# Revit family: Deca_Ducha Higienica com Derivacao_Ducha Activa Competitivo_1948.ACT.CR
name_source: partatom
category: Plumbing Fixtures
units: mm (PartAtom-declared; Revit-internal decimal feet)

## family parameters
Cut with Voids When Loaded = No
Host = Face
Part Type = Normal
Room Calculation Point = No
Round Connector Dimension = Use Radius
Shared = No

## types (2) — shared parameters
Acompanha o Produto = Acompanha Parfuso e Bucha para fixação + Deca confort
Aprovado por = quattroD
Atendimento ao Cliente = 0800-0117073
Categoria = METAIS PARA BANHEIRO
Composição Anel Vedação = -
Composição Assento = -
Composição Básica = Liga cobre (bronze e latão),Aço,Plástico de Engenharia,Elastômeros
Composição Componente = -
Consumo = -
Cor Interna = -
Cor Secundária = -
Cores Componente = -
Criado por = quattroD
Código Pai = 1948.ACT.CR
Default Elevation = 1200 mm
Description = Ducha higiênica universal com derivação
Diâmetro Água Fria = 15 mm  [stored 0.0492126 ft]
Informações Complementares = -
Itens de Instalação = -
Linha = Ducha Activa Competitivo
Manufacturer = Deca
Norma = NBR14877
Pressão máx. funcionamento = 40 MCA
Pressão mín. Aquec. Acúmulo = -
Pressão mín. Aquec. Passagem = -
Pressão mín. funcionamento = 2 MCA
Raio Água Fria = 8 mm  [stored 0.0262467 ft]
Saída de Esgoto = -
Segmento = Banheiro Competitivo
Tipo de dispositivo economizador = Sim
Tipo de mecanismo utilizado = -
Tipo de rosca de entrada = BSP NBR 8133
Tipo de rosca de saída = -
URL = www.deca.com.br
Vazão na Pressão máx. (L/min) = 6
Vazão na Pressão mín. (L/min) = 4

## per-type parameters (varying)
| type | Cor Principal | Material | Model | Peso Líquido (Kg) |
| 1948.C.ACT.BR_Branco | Branco | Deca_Branco | 1948.C.ACT.BR | 0.67 |
| 1948.C.ACT.CR_Cromado | Cromado | Deca_Cromado | 1948.C.ACT.CR | 0.653 |

note: source unit labels omitted for Vazão na Pressão máx. (L/min), Vazão na Pressão mín. (L/min) — the stored unit's dimension contradicts the parameter name (converter mislabeling)

note: [stored X ft] marks values corroborated as IEEE doubles in the binary element streams (Revit-internal decimal feet)

## geometry (parser evidence)
native form markers: Sweep x2
no freeform markers — native parametric forms only
